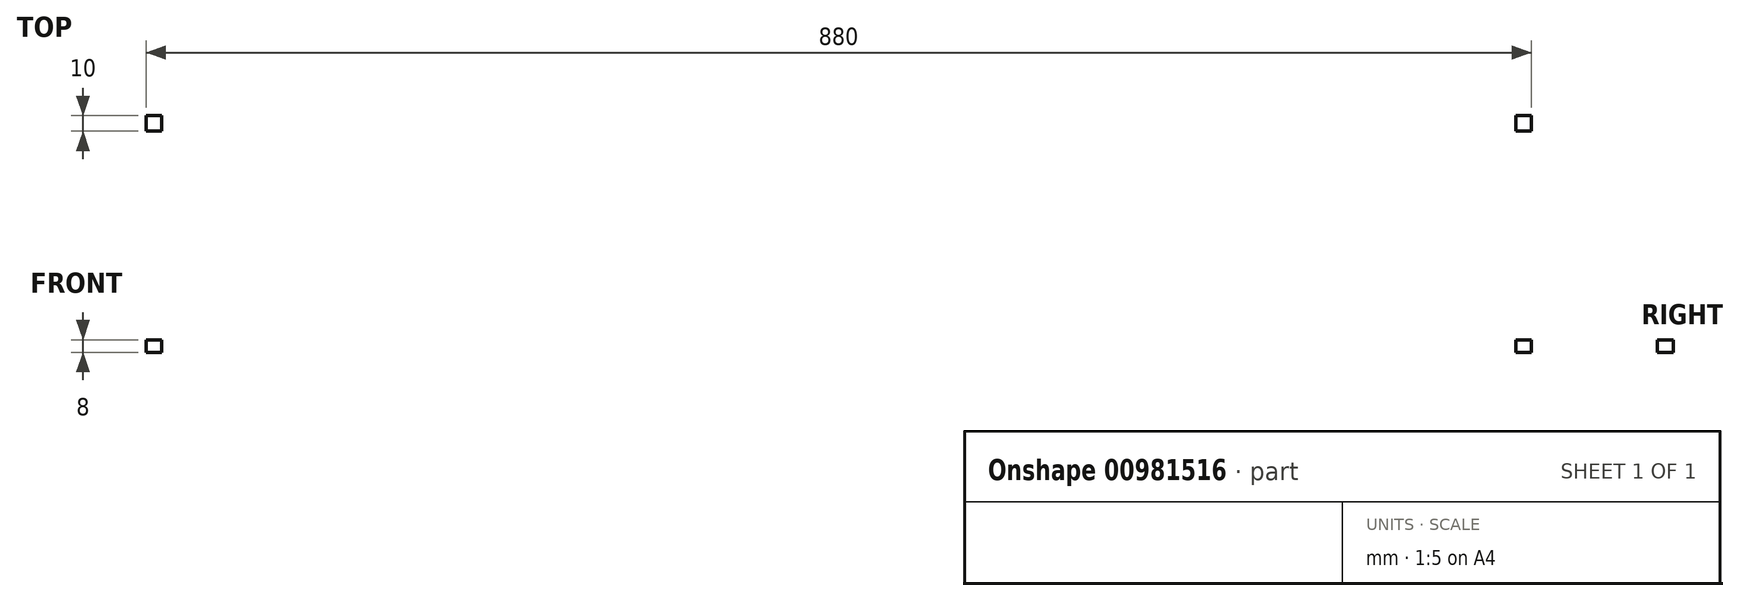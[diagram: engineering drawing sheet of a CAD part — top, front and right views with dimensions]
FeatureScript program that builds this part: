
annotation { "Feature Type Name" : "Feature", "Feature Type Description" : "" }
export const myFeature = defineFeature(function(context is Context, id is Id, definition is map)
    precondition{}
    {
        {
            var Q0;
            Q0=qCreatedBy(makeId("Top.planeOp"),FACE);
            var sketch = newSketch(context, id + "F0", { "sketchPlane" : qUnion([Q0])});
            skLineSegment(sketch, "E0.bottom", {"start": v(-235.88, 119.23) * mm, "end": v(644.12, 119.23) * mm});
            skLineSegment(sketch, "E0.top", {"start": v(-235.88, -130.77) * mm, "end": v(644.12, -130.77) * mm});
            skLineSegment(sketch, "E0.left", {"start": v(-235.88, 119.23) * mm, "end": v(-235.88, -130.77) * mm});
            skLineSegment(sketch, "E0.right", {"start": v(644.12, 119.23) * mm, "end": v(644.12, -130.77) * mm});
            skLineSegment(sketch, "E1.bottom", {"start": v(-235.88, 119.23) * mm, "end": v(-225.88, 119.23) * mm});
            skLineSegment(sketch, "E1.top", {"start": v(-235.88, 109.23) * mm, "end": v(-225.88, 109.23) * mm});
            skLineSegment(sketch, "E1.left", {"start": v(-235.88, 119.23) * mm, "end": v(-235.88, 109.23) * mm});
            skLineSegment(sketch, "E1.right", {"start": v(-225.88, 119.23) * mm, "end": v(-225.88, 109.23) * mm});
            skLineSegment(sketch, "E2.bottom", {"start": v(-235.88, -130.77) * mm, "end": v(-225.88, -130.77) * mm});
            skLineSegment(sketch, "E2.top", {"start": v(-235.88, -120.77) * mm, "end": v(-225.88, -120.77) * mm});
            skLineSegment(sketch, "E2.left", {"start": v(-235.88, -130.77) * mm, "end": v(-235.88, -120.77) * mm});
            skLineSegment(sketch, "E2.right", {"start": v(-225.88, -130.77) * mm, "end": v(-225.88, -120.77) * mm});
            skLineSegment(sketch, "E3.bottom", {"start": v(644.12, -130.77) * mm, "end": v(634.12, -130.77) * mm});
            skLineSegment(sketch, "E3.top", {"start": v(644.12, -120.77) * mm, "end": v(634.12, -120.77) * mm});
            skLineSegment(sketch, "E3.left", {"start": v(644.12, -130.77) * mm, "end": v(644.12, -120.77) * mm});
            skLineSegment(sketch, "E3.right", {"start": v(634.12, -130.77) * mm, "end": v(634.12, -120.77) * mm});
            skLineSegment(sketch, "E4.bottom", {"start": v(644.12, 119.23) * mm, "end": v(634.12, 119.23) * mm});
            skLineSegment(sketch, "E4.top", {"start": v(644.12, 109.23) * mm, "end": v(634.12, 109.23) * mm});
            skLineSegment(sketch, "E4.left", {"start": v(644.12, 119.23) * mm, "end": v(644.12, 109.23) * mm});
            skLineSegment(sketch, "E4.right", {"start": v(634.12, 119.23) * mm, "end": v(634.12, 109.23) * mm});
            skSolve(sketch);
        }
        {
            var Q0;
            Q0=makeQuery(id+"F0.imprint","IMPRINT",FACE,{"disambiguationData":[TD([[makeQuery(id+"F0.imprint","IMPRINT",EDGE,{"derivedFrom":sQuery(id+"F0.wireOp",EDGE,"E0.bottom")}),-1.0]])]});
            extrude(context, id + "F1", {"entities" : qUnion([Q0]), "depth" : 8 * mm, "offsetDistance" : 25 * mm});
        }
    });
